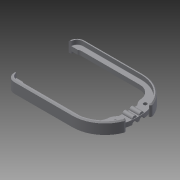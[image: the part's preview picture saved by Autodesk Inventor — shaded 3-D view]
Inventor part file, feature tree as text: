
AUTODESK INVENTOR PART (.ipt)
format: ipt  version: 2014 SP1 (Build 180222100, 222)  size: 372,224 bytes
history: native  units: in
note: dims shown in document units (in); Inventor stores cm internally (conversion verified against a paired STEP export)
features: extrude x7, sketch x7, fillet x3, other x1, chamfer x1, projected_geometry x1
ambient origin geometry x8: Origin, YZ Plane, XZ Plane, XY Plane, X Axis, Y Axis, Z Axis, Center Point
bodies: Solid1 (feature_tree)
feature tree (20):
  other  "electronicsbox_top.ipt"
  extrude  "Extrusion1"  Depth=0.3937in TaperAngle=0.0deg
  extrude  "Extrusion2"  Depth=0.025in
  extrude  "Extrusion3"  Depth=0.025in
  extrude  "Extrusion4"  Depth=0.025in
  extrude  "Extrusion5"  Depth=0.125in
  extrude  "Extrusion6"  Depth=0.5in
  fillet  "Fillet1"  Radius=0.5in
  chamfer  "Chamfer1"  Distance=0.375in
  extrude  "Extrusion7"  Depth=0.02in
  fillet  "Fillet2"  Radius=0.1969in
  fillet  "Fillet3"  Radius=0.1969in
  sketch  "Sketch28"  dims[d28=0.2756in d29=0.2756in d31=0.1969in d32=0.1969in d33=0.375in d34=0.0in d35=0.2657in d36=0.2657in d37=0.1969in d38=0.1969in d39=0.75in d40=0.0in d41=0.125in d42=0.0625in d43=0.125in d44=45.0deg d45=0.1969in d46=0.1969in d47=0.1969in d48=0.75in d49=0.0in d50=0.6875in d51=0.02in]
  sketch  "Sketch2"  dims[d0=0.3937in d1=0.25in d2=0.0in]
  sketch  "Sketch3"  dims[d7=0.25in d8=0.0in d9=0.025in]
  sketch  "Sketch5"  dims[d13=0.025in d14=0.025in]
  projected_geometry  "Projected Loop1"
  sketch  "Sketch6"  dims[d16=0.025in d17=0.025in]
  sketch  "Sketch7"  dims[d18=0.125in d19=0.125in]
  sketch  "Sketch8"  dims[d20=0.25in d21=0.0in d24=0.5in d25=0.5in d26=0.375in d27=0.0in]
